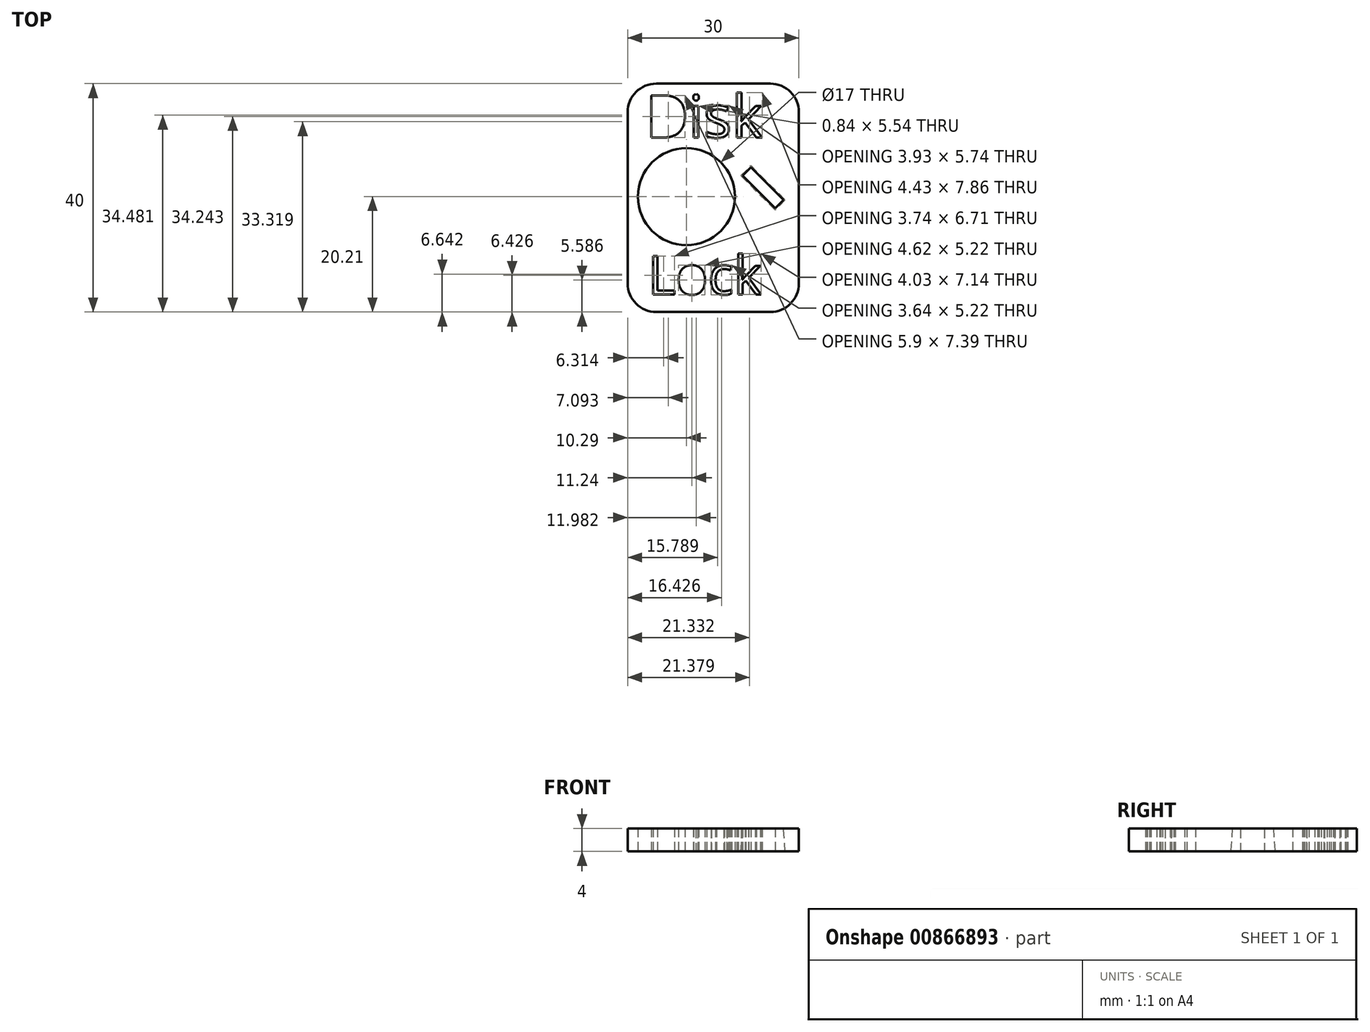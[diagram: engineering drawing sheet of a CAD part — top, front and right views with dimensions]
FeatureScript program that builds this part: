
annotation { "Feature Type Name" : "Feature", "Feature Type Description" : "" }
export const myFeature = defineFeature(function(context is Context, id is Id, definition is map)
    precondition{}
    {
        {
            var Q0;
            Q0=qCreatedBy(makeId("Top.planeOp"),FACE);
            var sketch = newSketch(context, id + "F0", { "sketchPlane" : qUnion([Q0])});
            skLineSegment(sketch, "E0.bottom", {"start": v(-5.29, 0) * mm, "end": v(14.71, 0) * mm});
            skLineSegment(sketch, "E0.top", {"start": v(-5.29, -40) * mm, "end": v(14.71, -40) * mm});
            skLineSegment(sketch, "E0.left", {"start": v(-10.29, -5) * mm, "end": v(-10.29, -35) * mm});
            skLineSegment(sketch, "E0.right", {"start": v(19.71, -5) * mm, "end": v(19.71, -35) * mm});
            skText(sketch, "E1", { "text": "Disk\n", "fontName": "OpenSans-Regular.ttf"});
            skText(sketch, "E2", { "text": "Lock\n", "fontName": "OpenSans-Regular.ttf"});
            skCircle(sketch, "E3", {"center": v(0, -19.79) * mm, "radius": 8.5 * mm});
            skPoint(sketch, "E4.visualSharp", {"position": v(19.71, 0) * mm});
            skArc(sketch, "E4.filletArc", {"start": v(19.71, -5) * mm, "mid": v(18.25, -1.46) * mm, "end": v(14.71, 0) * mm});
            skPoint(sketch, "E5.visualSharp", {"position": v(-10.29, 0) * mm});
            skArc(sketch, "E5.filletArc", {"start": v(-5.29, 0) * mm, "mid": v(-8.82, -1.46) * mm, "end": v(-10.29, -5) * mm});
            skPoint(sketch, "E6.visualSharp", {"position": v(19.71, -40) * mm});
            skArc(sketch, "E6.filletArc", {"start": v(14.71, -40) * mm, "mid": v(18.25, -38.54) * mm, "end": v(19.71, -35) * mm});
            skPoint(sketch, "E7.visualSharp", {"position": v(-10.29, -40) * mm});
            skArc(sketch, "E7.filletArc", {"start": v(-10.29, -35) * mm, "mid": v(-8.82, -38.54) * mm, "end": v(-5.29, -40) * mm});
            const initialGuessF0  = {"E1": [-0.00716, -0.00945, 1, 0, 0.00745], "E2": [-0.00677, -0.03693, 1, 0, 0.00677]};
            skSetInitialGuess(sketch, initialGuessF0);
            skSolve(sketch);
        }
        {
            var Q0;
            Q0 = qSketchRegion(id + "F0", true);
            extrude(context, id + "F1", {"entities" : qUnion([Q0]), "depth" : 4 * mm, "offsetDistance" : 25 * mm});
        }
        {
            var Q0;
            Q0=makeQuery(id+"F1.opExtrude","CAP_FACE",FACE,{"disambiguationData":[OSD([sQuery(id+"F0.wireOp",EDGE,"E0.bottom"),sQuery(id+"F0.wireOp",EDGE,"E0.top"),sQuery(id+"F0.wireOp",EDGE,"E0.left"),sQuery(id+"F0.wireOp",EDGE,"E0.right"),sQuery(id+"F0.wireOp",EDGE,"E1.sketch_text.stroke-0"),sQuery(id+"F0.wireOp",EDGE,"E1.sketch_text.stroke-1"),sQuery(id+"F0.wireOp",EDGE,"E1.sketch_text.stroke-2"),sQuery(id+"F0.wireOp",EDGE,"E1.sketch_text.stroke-3"),sQuery(id+"F0.wireOp",EDGE,"E1.sketch_text.stroke-4"),sQuery(id+"F0.wireOp",EDGE,"E1.sketch_text.stroke-5"),sQuery(id+"F0.wireOp",EDGE,"E1.sketch_text.stroke-6"),sQuery(id+"F0.wireOp",EDGE,"E1.sketch_text.stroke-14"),sQuery(id+"F0.wireOp",EDGE,"E1.sketch_text.stroke-15"),sQuery(id+"F0.wireOp",EDGE,"E1.sketch_text.stroke-16"),sQuery(id+"F0.wireOp",EDGE,"E1.sketch_text.stroke-17"),sQuery(id+"F0.wireOp",EDGE,"E1.sketch_text.stroke-18"),sQuery(id+"F0.wireOp",EDGE,"E1.sketch_text.stroke-19"),sQuery(id+"F0.wireOp",EDGE,"E1.sketch_text.stroke-20"),sQuery(id+"F0.wireOp",EDGE,"E1.sketch_text.stroke-21"),sQuery(id+"F0.wireOp",EDGE,"E1.sketch_text.stroke-22"),sQuery(id+"F0.wireOp",EDGE,"E1.sketch_text.stroke-23"),sQuery(id+"F0.wireOp",EDGE,"E1.sketch_text.stroke-24"),sQuery(id+"F0.wireOp",EDGE,"E1.sketch_text.stroke-25"),sQuery(id+"F0.wireOp",EDGE,"E1.sketch_text.stroke-26"),sQuery(id+"F0.wireOp",EDGE,"E1.sketch_text.stroke-27"),sQuery(id+"F0.wireOp",EDGE,"E1.sketch_text.stroke-28"),sQuery(id+"F0.wireOp",EDGE,"E1.sketch_text.stroke-29"),sQuery(id+"F0.wireOp",EDGE,"E1.sketch_text.stroke-30"),sQuery(id+"F0.wireOp",EDGE,"E1.sketch_text.stroke-31"),sQuery(id+"F0.wireOp",EDGE,"E1.sketch_text.stroke-32"),sQuery(id+"F0.wireOp",EDGE,"E1.sketch_text.stroke-33"),sQuery(id+"F0.wireOp",EDGE,"E1.sketch_text.stroke-34"),sQuery(id+"F0.wireOp",EDGE,"E1.sketch_text.stroke-35"),sQuery(id+"F0.wireOp",EDGE,"E1.sketch_text.stroke-36"),sQuery(id+"F0.wireOp",EDGE,"E1.sketch_text.stroke-37"),sQuery(id+"F0.wireOp",EDGE,"E1.sketch_text.stroke-38"),sQuery(id+"F0.wireOp",EDGE,"E1.sketch_text.stroke-39"),sQuery(id+"F0.wireOp",EDGE,"E1.sketch_text.stroke-40"),sQuery(id+"F0.wireOp",EDGE,"E1.sketch_text.stroke-41"),sQuery(id+"F0.wireOp",EDGE,"E1.sketch_text.stroke-42"),sQuery(id+"F0.wireOp",EDGE,"E1.sketch_text.stroke-43"),sQuery(id+"F0.wireOp",EDGE,"E1.sketch_text.stroke-44"),sQuery(id+"F0.wireOp",EDGE,"E1.sketch_text.stroke-45"),sQuery(id+"F0.wireOp",EDGE,"E1.sketch_text.stroke-46"),sQuery(id+"F0.wireOp",EDGE,"E1.sketch_text.stroke-47"),sQuery(id+"F0.wireOp",EDGE,"E1.sketch_text.stroke-48"),sQuery(id+"F0.wireOp",EDGE,"E1.sketch_text.stroke-49"),sQuery(id+"F0.wireOp",EDGE,"E1.sketch_text.stroke-50"),sQuery(id+"F0.wireOp",EDGE,"E1.sketch_text.stroke-51"),sQuery(id+"F0.wireOp",EDGE,"E1.sketch_text.stroke-52"),sQuery(id+"F0.wireOp",EDGE,"E1.sketch_text.stroke-53"),sQuery(id+"F0.wireOp",EDGE,"E1.sketch_text.stroke-54"),sQuery(id+"F0.wireOp",EDGE,"E1.sketch_text.stroke-55"),sQuery(id+"F0.wireOp",EDGE,"E1.sketch_text.stroke-56"),sQuery(id+"F0.wireOp",EDGE,"E1.sketch_text.stroke-57"),sQuery(id+"F0.wireOp",EDGE,"E1.sketch_text.stroke-58"),sQuery(id+"F0.wireOp",EDGE,"E1.sketch_text.stroke-59"),sQuery(id+"F0.wireOp",EDGE,"E1.sketch_text.stroke-60"),sQuery(id+"F0.wireOp",EDGE,"E1.sketch_text.stroke-61"),sQuery(id+"F0.wireOp",EDGE,"E1.sketch_text.stroke-62"),sQuery(id+"F0.wireOp",EDGE,"E1.sketch_text.stroke-63"),sQuery(id+"F0.wireOp",EDGE,"E1.sketch_text.stroke-64"),sQuery(id+"F0.wireOp",EDGE,"E1.sketch_text.stroke-65"),sQuery(id+"F0.wireOp",EDGE,"E2.sketch_text.stroke-0"),sQuery(id+"F0.wireOp",EDGE,"E2.sketch_text.stroke-1"),sQuery(id+"F0.wireOp",EDGE,"E2.sketch_text.stroke-2"),sQuery(id+"F0.wireOp",EDGE,"E2.sketch_text.stroke-3"),sQuery(id+"F0.wireOp",EDGE,"E2.sketch_text.stroke-4"),sQuery(id+"F0.wireOp",EDGE,"E2.sketch_text.stroke-5"),sQuery(id+"F0.wireOp",EDGE,"E2.sketch_text.stroke-6"),sQuery(id+"F0.wireOp",EDGE,"E2.sketch_text.stroke-7"),sQuery(id+"F0.wireOp",EDGE,"E2.sketch_text.stroke-8"),sQuery(id+"F0.wireOp",EDGE,"E2.sketch_text.stroke-9"),sQuery(id+"F0.wireOp",EDGE,"E2.sketch_text.stroke-10"),sQuery(id+"F0.wireOp",EDGE,"E2.sketch_text.stroke-11"),sQuery(id+"F0.wireOp",EDGE,"E2.sketch_text.stroke-12"),sQuery(id+"F0.wireOp",EDGE,"E2.sketch_text.stroke-13"),sQuery(id+"F0.wireOp",EDGE,"E2.sketch_text.stroke-14"),sQuery(id+"F0.wireOp",EDGE,"E2.sketch_text.stroke-23"),sQuery(id+"F0.wireOp",EDGE,"E2.sketch_text.stroke-24"),sQuery(id+"F0.wireOp",EDGE,"E2.sketch_text.stroke-25"),sQuery(id+"F0.wireOp",EDGE,"E2.sketch_text.stroke-26"),sQuery(id+"F0.wireOp",EDGE,"E2.sketch_text.stroke-27"),sQuery(id+"F0.wireOp",EDGE,"E2.sketch_text.stroke-28"),sQuery(id+"F0.wireOp",EDGE,"E2.sketch_text.stroke-29"),sQuery(id+"F0.wireOp",EDGE,"E2.sketch_text.stroke-30"),sQuery(id+"F0.wireOp",EDGE,"E2.sketch_text.stroke-31"),sQuery(id+"F0.wireOp",EDGE,"E2.sketch_text.stroke-32"),sQuery(id+"F0.wireOp",EDGE,"E2.sketch_text.stroke-33"),sQuery(id+"F0.wireOp",EDGE,"E2.sketch_text.stroke-34"),sQuery(id+"F0.wireOp",EDGE,"E2.sketch_text.stroke-35"),sQuery(id+"F0.wireOp",EDGE,"E2.sketch_text.stroke-36"),sQuery(id+"F0.wireOp",EDGE,"E2.sketch_text.stroke-37"),sQuery(id+"F0.wireOp",EDGE,"E2.sketch_text.stroke-38"),sQuery(id+"F0.wireOp",EDGE,"E2.sketch_text.stroke-39"),sQuery(id+"F0.wireOp",EDGE,"E2.sketch_text.stroke-40"),sQuery(id+"F0.wireOp",EDGE,"E2.sketch_text.stroke-41"),sQuery(id+"F0.wireOp",EDGE,"E2.sketch_text.stroke-42"),sQuery(id+"F0.wireOp",EDGE,"E2.sketch_text.stroke-43"),sQuery(id+"F0.wireOp",EDGE,"E2.sketch_text.stroke-44"),sQuery(id+"F0.wireOp",EDGE,"E2.sketch_text.stroke-45"),sQuery(id+"F0.wireOp",EDGE,"E2.sketch_text.stroke-46"),sQuery(id+"F0.wireOp",EDGE,"E2.sketch_text.stroke-47"),sQuery(id+"F0.wireOp",EDGE,"E2.sketch_text.stroke-48"),sQuery(id+"F0.wireOp",EDGE,"E2.sketch_text.stroke-49"),sQuery(id+"F0.wireOp",EDGE,"E2.sketch_text.stroke-50"),sQuery(id+"F0.wireOp",EDGE,"E2.sketch_text.stroke-51"),sQuery(id+"F0.wireOp",EDGE,"E2.sketch_text.stroke-52"),sQuery(id+"F0.wireOp",EDGE,"E3"),sQuery(id+"F0.wireOp",EDGE,"E4.filletArc"),sQuery(id+"F0.wireOp",EDGE,"E5.filletArc"),sQuery(id+"F0.wireOp",EDGE,"E6.filletArc"),sQuery(id+"F0.wireOp",EDGE,"E7.filletArc")])],"isStart":true});
            var sketch = newSketch(context, id + "F2", { "sketchPlane" : qUnion([Q0])});
            skLineSegment(sketch, "E8.bottom", {"start": v(17.3, 20.38) * mm, "end": v(11.3, 14.36) * mm});
            skLineSegment(sketch, "E8.top", {"start": v(15.54, 22.14) * mm, "end": v(9.53, 16.13) * mm});
            skLineSegment(sketch, "E8.left", {"start": v(17.3, 20.38) * mm, "end": v(15.54, 22.14) * mm});
            skLineSegment(sketch, "E8.right", {"start": v(11.3, 14.36) * mm, "end": v(9.53, 16.13) * mm});
            skPoint(sketch, "E8.middle", {"position": v(13.13, 16.14) * mm});
            skPoint(sketch, "E8.middle.positionSnap0", {"position": v(19.71, 20) * mm});
            skPoint(sketch, "E8.centerSnap0", {"position": v(19.71, 20) * mm});
            skSolve(sketch);
        }
        {
            var Q0;
            Q0 = qSketchRegion(id + "F2", true);
            extrude(context, id + "F3", {"entities" : qUnion([Q0]), "operationType" : NewBodyOperationType.REMOVE, "oppositeDirection" : true, "depth" : 5 * mm, "offsetDistance" : 25 * mm, "hasDraft" : true, "draftAngle" : 3 * degree, "draftPullDirection" : true});
        }
    });
